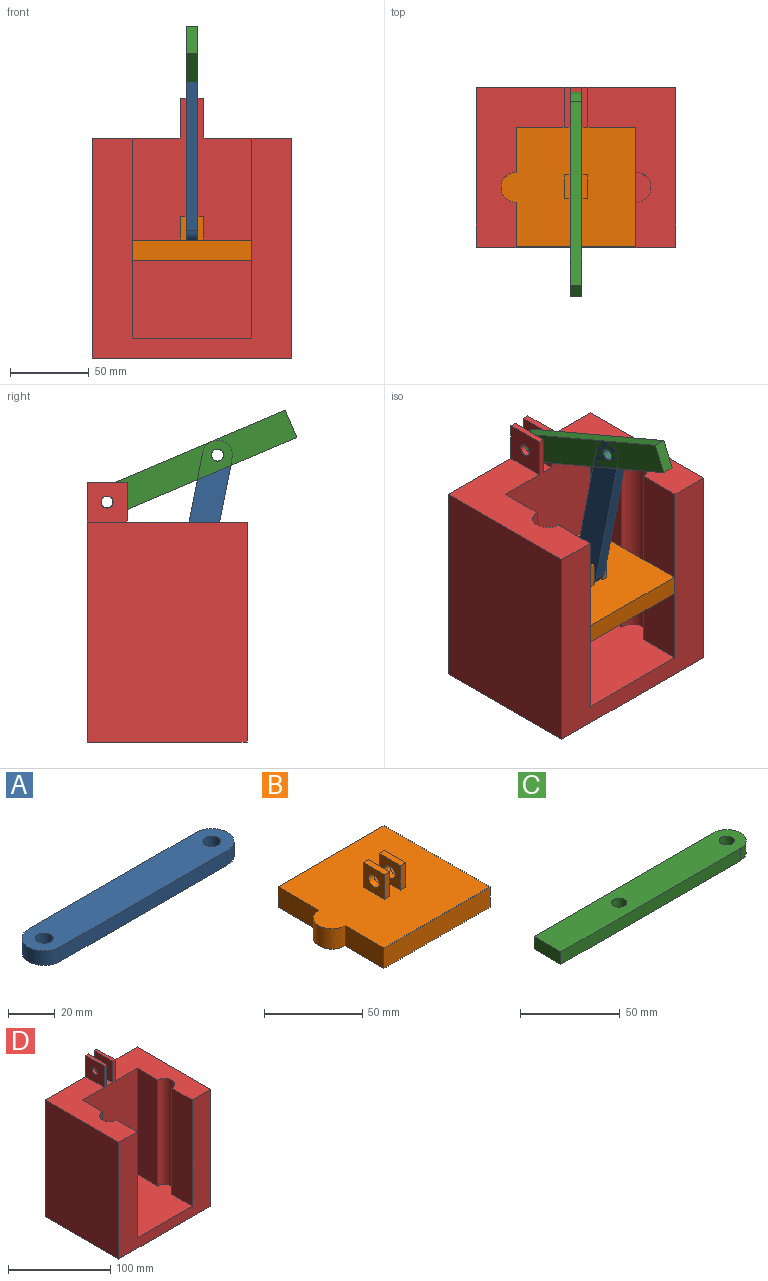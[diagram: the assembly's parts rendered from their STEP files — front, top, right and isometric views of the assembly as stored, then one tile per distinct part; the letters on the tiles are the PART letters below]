
ASSEMBLY  parts=4 mates=4
PART A: 8 faces, bbox 120.7x19.1x7.6 mm
  f0: cylinder r=9.53mm len=19.05mm, axis (0,0,-1), area 228mm2, adj f1,f4,f6,f7
  f1: plane 101.6x7.62mm, normal (0,-1,0), area 774.2mm2, adj f0,f2,f6,f7
  f2: cylinder r=9.53mm len=19.05mm, axis (0,0,-1), area 228mm2, adj f1,f4,f6,f7
  f3: cylinder r=3.81mm len=7.62mm, axis (0,0,-1), area 182.4mm2, adj f6,f7
  f4: plane 101.6x7.62mm, normal (0,1,0), area 774.2mm2, adj f0,f2,f6,f7
  f5: cylinder r=3.81mm len=7.62mm, axis (0,0,-1), area 182.4mm2, adj f6,f7
  f6: plane 120.65x19.05mm, normal (0,0,1), area 2129.3mm2, adj f0,f1,f2,f3,f4,f5
  f7: plane 120.65x19.05mm, normal (0,0,-1), area 2129.3mm2, adj f0,f1,f2,f3,f4,f5
PART B: 20 faces, bbox 85.7x76.2x27.9 mm
  f0: plane 85.73x76.2mm, normal (0,0,1), area 5832.8mm2, adj f1,f2,f3,f4,f5,f7,f8,f9
  f1: plane 27.93x12.7mm, normal (-1,0,0), area 354.7mm2, adj f0,f2,f6,f7
  f2: plane 76.2x12.7mm, normal (0,-1,0), area 967.7mm2, adj f0,f1,f3,f6
  f3: plane 76.2x12.7mm, normal (1,0,0), area 967.7mm2, adj f0,f2,f4,f6
  f4: plane 76.2x12.7mm, normal (0,1,0), area 967.7mm2, adj f0,f3,f5,f6
  f5: plane 29.22x12.7mm, normal (-1,0,0), area 371.1mm2, adj f0,f4,f6,f7
  f6: plane 85.73x76.2mm, normal (0,0,-1), area 5949mm2, adj f1,f2,f3,f4,f5,f7
  f7: cylinder r=9.53mm len=19.05mm, axis (0,0,1), area 380mm2, adj f0,f1,f5,f6
  f8: plane 15.24x3.81mm, normal (0,-1,0), area 58.1mm2, adj f0,f9,f11,f12
  f9: plane 15.24x15.24mm, normal (1,0,0), area 186.7mm2, adj f0,f8,f10,f12,f19
  f10: plane 15.24x3.81mm, normal (0,1,0), area 58.1mm2, adj f0,f9,f11,f12
  f11: plane 15.24x15.24mm, normal (-1,0,0), area 186.7mm2, adj f0,f8,f10,f12,f19
  f12: plane 15.24x3.81mm, normal (0,0,1), area 58.1mm2, adj f8,f9,f10,f11
  f13: plane 15.24x15.24mm, normal (-1,0,0), area 186.7mm2, adj f0,f14,f16,f17,f18
  f14: plane 15.24x3.81mm, normal (0,-1,0), area 58.1mm2, adj f0,f13,f15,f17
  f15: plane 15.24x15.24mm, normal (1,0,0), area 186.7mm2, adj f0,f14,f16,f17,f18
  f16: plane 15.24x3.81mm, normal (0,1,0), area 58.1mm2, adj f0,f13,f15,f17
  f17: plane 15.24x3.81mm, normal (0,0,1), area 58.1mm2, adj f13,f14,f15,f16
  f18: cylinder r=3.81mm len=7.62mm, axis (-1,0,0), area 91.2mm2, adj f13,f15
  f19: cylinder r=3.81mm len=7.62mm, axis (-1,0,0), area 91.2mm2, adj f9,f11
PART C: 8 faces, bbox 136.5x19.1x7.6 mm
  f0: plane 127x7.62mm, normal (0,-1,0), area 967.7mm2, adj f1,f4,f6,f7
  f1: cylinder r=9.53mm len=19.05mm, axis (0,0,-1), area 228mm2, adj f0,f2,f6,f7
  f2: plane 127x7.62mm, normal (0,1,0), area 967.7mm2, adj f1,f4,f6,f7
  f3: cylinder r=3.81mm len=7.62mm, axis (0,0,-1), area 182.4mm2, adj f6,f7
  f4: plane 19.05x7.62mm, normal (-1,0,0), area 145.2mm2, adj f0,f2,f6,f7
  f5: cylinder r=3.81mm len=7.62mm, axis (0,0,-1), area 182.4mm2, adj f6,f7
  f6: plane 136.53x19.05mm, normal (0,0,1), area 2470.7mm2, adj f0,f1,f2,f3,f4,f5
  f7: plane 136.53x19.05mm, normal (0,0,-1), area 2470.7mm2, adj f0,f1,f2,f3,f4,f5
PART D: 24 faces, bbox 127x101.6x165.1 mm
  f0: plane 25.4x7.62mm, normal (0,0,1), area 193.5mm2, adj f5,f11,f17,f20
  f1: plane 101.6x55.88mm, normal (0,0,1), area 3212.3mm2, adj f2,f3,f4,f5,f7,f11,f12,f19
  f2: cylinder r=9.53mm len=127mm, axis (0,0,-1), area 3800.3mm2, adj f1,f3,f12,f14
  f3: plane 127x28.58mm, normal (-1,0,0), area 3629mm2, adj f1,f2,f7,f14
  f4: plane 139.7x101.6mm, normal (1,0,0), area 14193.5mm2, adj f1,f5,f7,f15
  f5: plane 165.1x127mm, normal (0,1,0), area 17935.4mm2, adj f0,f1,f4,f6,f13,f15,f16,f17
  f6: plane 139.7x101.6mm, normal (-1,0,0), area 14193.5mm2, adj f5,f7,f13,f15
  f7: plane 139.7x127mm, normal (0,-1,0), area 8064.5mm2, adj f1,f3,f4,f6,f8,f13,f14,f15
  f8: plane 127x28.58mm, normal (1,0,0), area 3629mm2, adj f7,f9,f13,f14
  f9: cylinder r=9.53mm len=127mm, axis (0,0,-1), area 3800.3mm2, adj f8,f10,f13,f14
  f10: plane 127x28.58mm, normal (1,0,0), area 3629mm2, adj f9,f11,f13,f14
  f11: plane 152.4x76.2mm, normal (0,-1,0), area 9870.9mm2, adj f0,f1,f10,f12,f13,f14,f16,f17
  f12: plane 127x28.58mm, normal (-1,0,0), area 3629mm2, adj f1,f2,f11,f14
  f13: plane 101.6x55.88mm, normal (0,0,1), area 3212.3mm2, adj f5,f6,f7,f8,f9,f10,f11,f16
  f14: plane 95.25x76.2mm, normal (0,0,1), area 6091.5mm2, adj f2,f3,f7,f8,f9,f10,f11,f12
  f15: plane 127x101.6mm, normal (0,0,-1), area 12903.2mm2, adj f4,f5,f6,f7
  f16: plane 25.4x25.4mm, normal (-1,0,0), area 599.6mm2, adj f5,f11,f13,f18,f23
  f17: plane 25.4x25.4mm, normal (1,0,0), area 599.6mm2, adj f0,f5,f11,f18,f23
  f18: plane 25.4x3.81mm, normal (0,0,1), area 96.8mm2, adj f5,f11,f16,f17
  f19: plane 25.4x25.4mm, normal (1,0,0), area 599.6mm2, adj f1,f5,f11,f21,f22
  f20: plane 25.4x25.4mm, normal (-1,0,0), area 599.6mm2, adj f0,f5,f11,f21,f22
  f21: plane 25.4x3.81mm, normal (0,0,1), area 96.8mm2, adj f5,f11,f19,f20
  f22: cylinder r=3.81mm len=7.62mm, axis (-1,0,0), area 91.2mm2, adj f19,f20
  f23: cylinder r=3.81mm len=7.62mm, axis (-1,0,0), area 91.2mm2, adj f16,f17
PLACE A rot(axis=(0.1,-0.99,-0.1),90.5deg) t=(-42.66,-37.63,149.07)mm
PLACE B t=(-24.16,1.76,54.27)mm
PLACE C rot(axis=(0.48,0.73,0.48),107.7deg) t=(-50.28,6.89,153.53)mm
PLACE D t=(-45.09,-12.29,4.78)mm fixed
MATE slider B.f7 <-> D.f9  axis (0,0,1) through (-84.57,1.76,66.97)mm
MATE revolute C.f1 <-> D.f22  axis (-1,0,0) through (-50.28,52.56,144.48)mm
MATE revolute A.f0 <-> B.f18  axis (-1,0,0) through (-50.28,2.02,74.59)mm
MATE revolute C.f3 <-> A.f2  axis (1,0,0) through (-42.66,-17.57,174.28)mm
